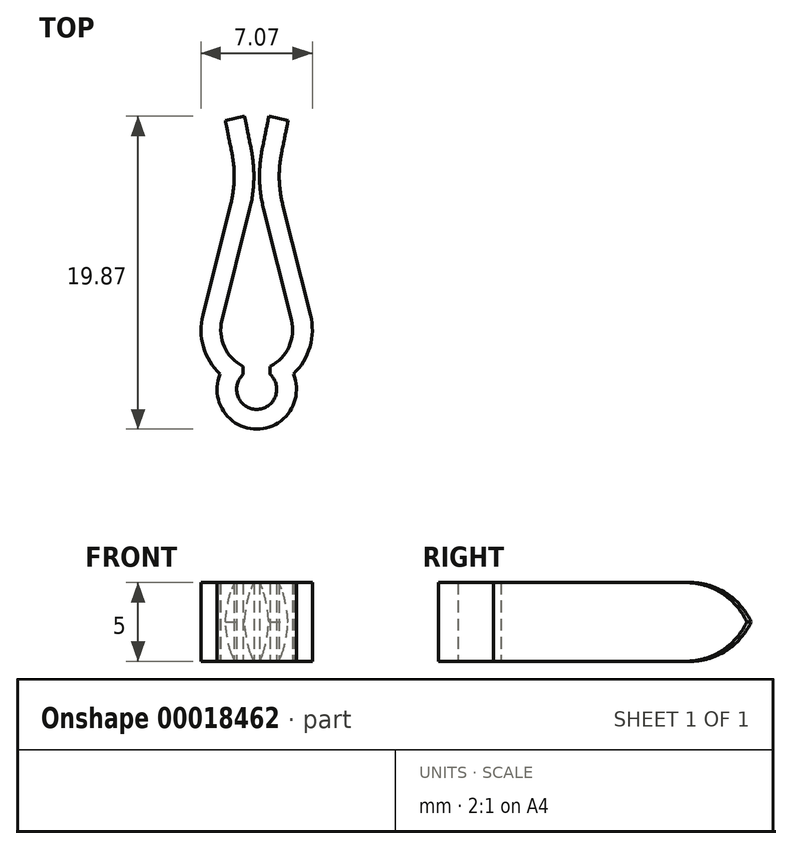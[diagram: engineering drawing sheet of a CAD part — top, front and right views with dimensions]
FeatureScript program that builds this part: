
annotation { "Feature Type Name" : "Feature", "Feature Type Description" : "" }
export const myFeature = defineFeature(function(context is Context, id is Id, definition is map)
    precondition{}
    {
        {
            var Q0;
            Q0=qCreatedBy(makeId("Top.planeOp"),FACE);
            var sketch = newSketch(context, id + "F0", { "sketchPlane" : qUnion([Q0])});
            skLineSegment(sketch, "E0", {"start": v(-14.92, 2.27) * mm, "end": v(-14.42, -0.2) * mm});
            skArc(sketch, "E1", {"start": v(-14.5, -3.45) * mm, "mid": v(-14.28, -1.83) * mm, "end": v(-14.42, -0.2) * mm});
            skLineSegment(sketch, "E2", {"start": v(-14.5, -3.45) * mm, "end": v(-16.26, -10.49) * mm});
            skArc(sketch, "E3", {"start": v(-16.26, -10.49) * mm, "mid": v(-16.23, -12.5) * mm, "end": v(-15.17, -14.23) * mm});
            skArc(sketch, "E4", {"start": v(-15.17, -14.23) * mm, "mid": v(-14.95, -16.6) * mm, "end": v(-12.85, -17.73) * mm});
            skLineSegment(sketch, "E5", {"start": v(-12.85, -19.86) * mm, "end": v(-12.85, 3.7) * mm, "construction": true});
            skArc(sketch, "E6.0", {"start": v(-13.14, -13.97) * mm, "mid": v(-14.11, -15.35) * mm, "end": v(-12.85, -16.48) * mm});
            skArc(sketch, "E6.1", {"start": v(-15.05, -10.79) * mm, "mid": v(-14.75, -12.78) * mm, "end": v(-13.14, -13.97) * mm});
            skLineSegment(sketch, "E6.2", {"start": v(-13.29, -3.76) * mm, "end": v(-15.05, -10.79) * mm});
            skArc(sketch, "E6.3", {"start": v(-13.29, -3.76) * mm, "mid": v(-13.03, -1.86) * mm, "end": v(-13.2, 0.05) * mm});
            skLineSegment(sketch, "E6.4", {"start": v(-13.7, 2.54) * mm, "end": v(-13.2, 0.05) * mm});
            skLineSegment(sketch, "E7", {"start": v(-14.92, 2.27) * mm, "end": v(-13.7, 2.54) * mm});
            skArc(sketch, "E8.MirrorCS", {"start": v(-9.43, -10.49) * mm, "mid": v(-9.47, -12.5) * mm, "end": v(-10.52, -14.23) * mm});
            skLineSegment(sketch, "E9.MirrorCS", {"start": v(-11.2, -3.45) * mm, "end": v(-9.43, -10.49) * mm});
            skLineSegment(sketch, "E10.MirrorCS", {"start": v(-12, 2.54) * mm, "end": v(-12.5, 0.05) * mm});
            skArc(sketch, "E11.MirrorCS", {"start": v(-12.4, -3.76) * mm, "mid": v(-12.66, -1.86) * mm, "end": v(-12.5, 0.05) * mm});
            skArc(sketch, "E12.MirrorCS", {"start": v(-11.2, -3.45) * mm, "mid": v(-11.41, -1.83) * mm, "end": v(-11.27, -0.2) * mm});
            skArc(sketch, "E13.MirrorCS", {"start": v(-10.64, -10.79) * mm, "mid": v(-10.94, -12.78) * mm, "end": v(-12.56, -13.97) * mm});
            skArc(sketch, "E14.MirrorCS", {"start": v(-12.56, -13.97) * mm, "mid": v(-11.58, -15.35) * mm, "end": v(-12.85, -16.48) * mm});
            skArc(sketch, "E15.MirrorCS", {"start": v(-10.52, -14.23) * mm, "mid": v(-10.74, -16.6) * mm, "end": v(-12.85, -17.73) * mm});
            skLineSegment(sketch, "E16.MirrorCS", {"start": v(-10.77, 2.27) * mm, "end": v(-12, 2.54) * mm});
            skLineSegment(sketch, "E17.MirrorCS", {"start": v(-12.4, -3.76) * mm, "end": v(-10.64, -10.79) * mm});
            skLineSegment(sketch, "E18.MirrorCS", {"start": v(-10.77, 2.27) * mm, "end": v(-11.27, -0.2) * mm});
            skCircle(sketch, "E19", {"center": v(-12.85, -15.32) * mm, "radius": 1 * mm});
            skSolve(sketch);
        }
        {
            var Q0;
            Q0=makeQuery(id+"F0.imprint","IMPRINT",FACE,{"disambiguationData":[TD([[makeQuery(id+"F0.imprint","IMPRINT",EDGE,{"derivedFrom":sQuery(id+"F0.wireOp",EDGE,"E0")}),1.0]])]});
            extrude(context, id + "F1", {"entities" : qUnion([Q0]), "depth" : 5 * mm});
        }
        {
            var Q0;
            Q0=makeQuery(id+"F1.opExtrude","CAP_EDGE",EDGE,{"disambiguationData":[OSD([sQuery(id+"F0.wireOp",EDGE,"E7")])],"isStart":false});
            var Q1;
            Q1=makeQuery(id+"F1.opExtrude","CAP_EDGE",EDGE,{"disambiguationData":[OSD([sQuery(id+"F0.wireOp",EDGE,"E16.MirrorCS")])],"isStart":false});
            var Q2;
            Q2=makeQuery(id+"F1.opExtrude","CAP_EDGE",EDGE,{"disambiguationData":[OSD([sQuery(id+"F0.wireOp",EDGE,"E16.MirrorCS")])],"isStart":true});
            var Q3;
            Q3=makeQuery(id+"F1.opExtrude","CAP_EDGE",EDGE,{"disambiguationData":[OSD([sQuery(id+"F0.wireOp",EDGE,"E7")])],"isStart":true});
            fillet(context, id + "F2", {"entities" : qUnion([Q0, Q1, Q2, Q3]), "radius" : 4.35 * mm, "tangentPropagation" : true, "allowEdgeOverflow" : false});
        }
        {
            var Q0;
            Q0=makeQuery(id+"F1.opExtrude","CAP_FACE",FACE,{"disambiguationData":[OSD([sQuery(id+"F0.wireOp",EDGE,"E0"),sQuery(id+"F0.wireOp",EDGE,"E1"),sQuery(id+"F0.wireOp",EDGE,"E2"),sQuery(id+"F0.wireOp",EDGE,"E3"),sQuery(id+"F0.wireOp",EDGE,"E4"),sQuery(id+"F0.wireOp",EDGE,"E6.0"),sQuery(id+"F0.wireOp",EDGE,"E6.1"),sQuery(id+"F0.wireOp",EDGE,"E6.2"),sQuery(id+"F0.wireOp",EDGE,"E6.3"),sQuery(id+"F0.wireOp",EDGE,"E6.4"),sQuery(id+"F0.wireOp",EDGE,"E7"),sQuery(id+"F0.wireOp",EDGE,"E8.MirrorCS"),sQuery(id+"F0.wireOp",EDGE,"E9.MirrorCS"),sQuery(id+"F0.wireOp",EDGE,"E10.MirrorCS"),sQuery(id+"F0.wireOp",EDGE,"E11.MirrorCS"),sQuery(id+"F0.wireOp",EDGE,"E12.MirrorCS"),sQuery(id+"F0.wireOp",EDGE,"E13.MirrorCS"),sQuery(id+"F0.wireOp",EDGE,"E14.MirrorCS"),sQuery(id+"F0.wireOp",EDGE,"E15.MirrorCS"),sQuery(id+"F0.wireOp",EDGE,"E16.MirrorCS"),sQuery(id+"F0.wireOp",EDGE,"E17.MirrorCS"),sQuery(id+"F0.wireOp",EDGE,"E18.MirrorCS")])],"isStart":false});
            var sketch = newSketch(context, id + "F3", { "sketchPlane" : qUnion([Q0])});
            skLineSegment(sketch, "E20", {"start": v(-13.14, -13.97) * mm, "end": v(-12.56, -13.97) * mm, "construction": true});
            skLineSegment(sketch, "E21", {"start": v(-12.85, -10.88) * mm, "end": v(-12.85, -13.97) * mm, "construction": true});
            skLineSegment(sketch, "E22.bottom", {"start": v(-13.7, -13) * mm, "end": v(-11.99, -13) * mm});
            skLineSegment(sketch, "E22.top", {"start": v(-13.7, -14.82) * mm, "end": v(-11.99, -14.82) * mm});
            skLineSegment(sketch, "E22.left", {"start": v(-13.7, -13) * mm, "end": v(-13.7, -14.82) * mm});
            skLineSegment(sketch, "E22.right", {"start": v(-11.99, -13) * mm, "end": v(-11.99, -14.82) * mm});
            skSolve(sketch);
        }
        {
            var Q0;
            {var subQ12=sQuery(id+"F3.wireOp",EDGE,"E22.bottom");Q0=makeQuery(id+"F3.imprint","IMPRINT",FACE,{"disambiguationData":[TD([[makeQuery(id+"F3.imprint","IMPRINT",EDGE,{"derivedFrom":subQ12}),-1.0]])]});}
            var Q1;
            {var subQ0=makeQuery(id+"F1.opExtrude","CAP_EDGE",EDGE,{"disambiguationData":[OSD([sQuery(id+"F0.wireOp",EDGE,"E6.1")])],"isStart":false});var subQ1=sQuery(id+"F3.wireOp",EDGE,"E22.left");var subQ2=makeQuery(id+"F3.imprint","INTERSECT",VERTEX,{"derivedFrom":[subQ0,subQ1]});Q1=makeQuery(id+"F3.imprint","IMPRINT",FACE,{"disambiguationData":[TD([[makeQuery(id+"F3.imprint","IMPRINT",EDGE,{"disambiguationData":[TD([[subQ2,-1.0]])],"derivedFrom":subQ1}),1.0]])]});}
            var Q2;
            {var subQ0=makeQuery(id+"F1.opExtrude","CAP_EDGE",EDGE,{"disambiguationData":[OSD([sQuery(id+"F0.wireOp",EDGE,"E13.MirrorCS")])],"isStart":false});var subQ1=sQuery(id+"F3.wireOp",EDGE,"E22.right");var subQ2=makeQuery(id+"F3.imprint","INTERSECT",VERTEX,{"derivedFrom":[subQ0,subQ1]});Q2=makeQuery(id+"F3.imprint","IMPRINT",FACE,{"disambiguationData":[TD([[makeQuery(id+"F3.imprint","IMPRINT",EDGE,{"disambiguationData":[TD([[subQ2,-1.0]])],"derivedFrom":subQ1}),-1.0]])]});}
            var Q3;
            Q3 = qSketchRegion(id + "F0", true);
            extrude(context, id + "F4", {"entities" : qUnion([Q0, Q1, Q2, Q3]), "operationType" : NewBodyOperationType.REMOVE, "oppositeDirection" : true, "depth" : 5 * mm});
        }
    });
